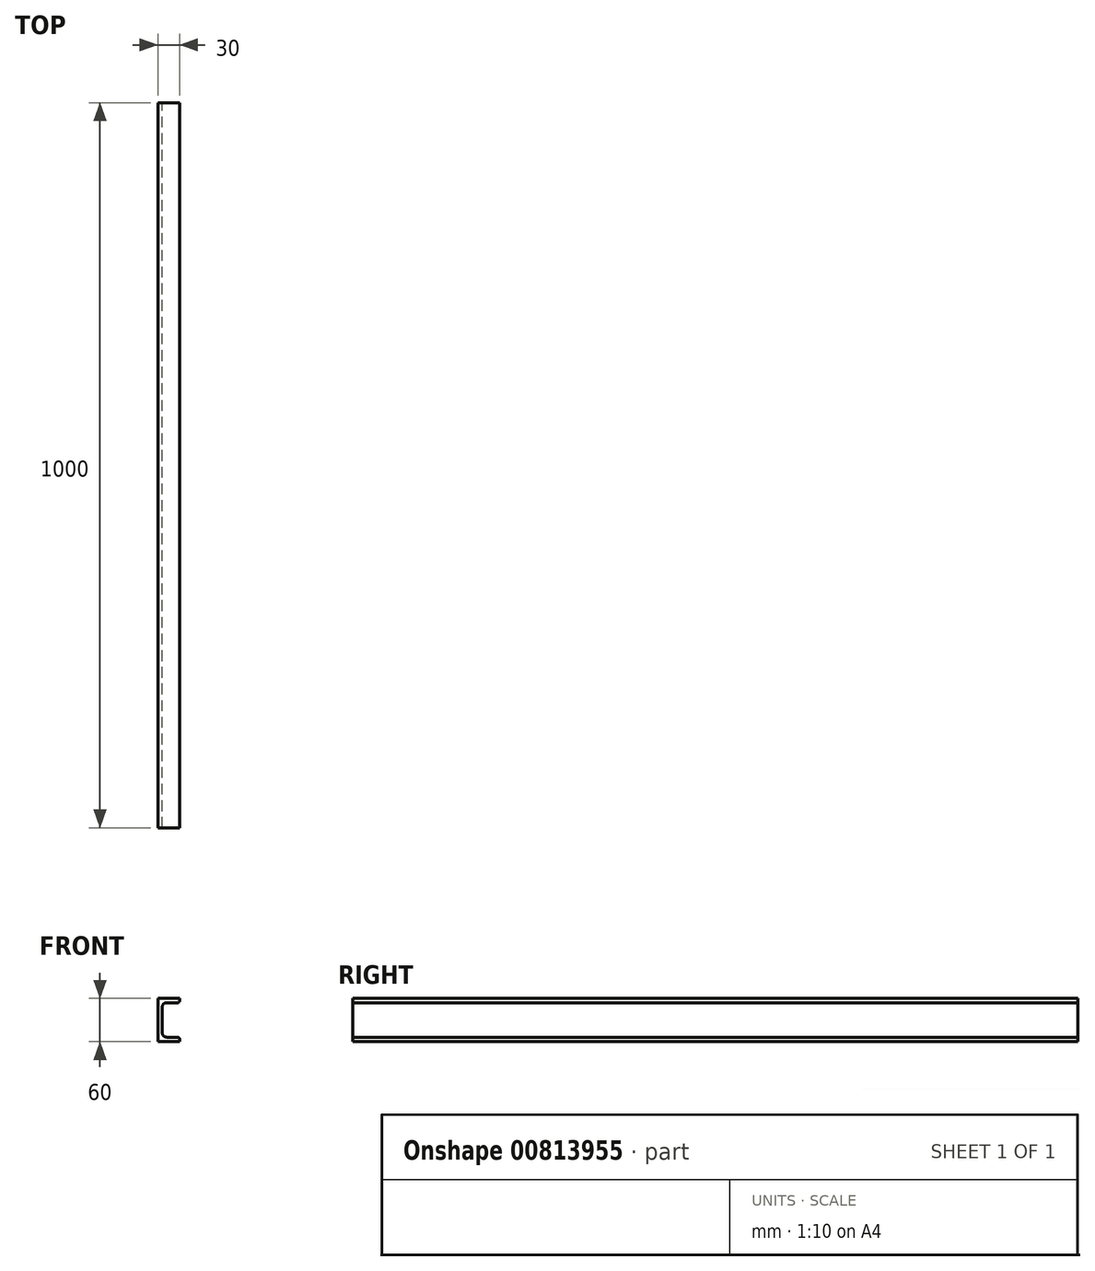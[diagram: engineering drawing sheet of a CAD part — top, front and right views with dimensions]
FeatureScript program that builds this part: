
annotation { "Feature Type Name" : "Feature", "Feature Type Description" : "" }
export const myFeature = defineFeature(function(context is Context, id is Id, definition is map)
    precondition{}
    {
        {
            var Q0;
            Q0=qCreatedBy(makeId("Front.planeOp"),FACE);
            var sketch = newSketch(context, id + "F0", { "sketchPlane" : qUnion([Q0])});
            skLineSegment(sketch, "E0", {"start": v(0, 0) * mm, "end": v(0, 60) * mm});
            skLineSegment(sketch, "E1", {"start": v(0, 60) * mm, "end": v(30, 60) * mm});
            skLineSegment(sketch, "E2", {"start": v(30, 60) * mm, "end": v(30, 56.75) * mm});
            skLineSegment(sketch, "E3", {"start": v(27, 53.75) * mm, "end": v(12, 53.75) * mm});
            skLineSegment(sketch, "E4", {"start": v(6, 47.75) * mm, "end": v(6, 12.25) * mm});
            skLineSegment(sketch, "E5", {"start": v(12, 6.25) * mm, "end": v(27, 6.25) * mm});
            skLineSegment(sketch, "E6", {"start": v(30, 3.25) * mm, "end": v(30, 0) * mm});
            skLineSegment(sketch, "E7", {"start": v(30, 0) * mm, "end": v(0, 0) * mm});
            skPoint(sketch, "E8.visualSharp", {"position": v(30, 53.75) * mm});
            skArc(sketch, "E8.filletArc", {"start": v(27, 53.75) * mm, "mid": v(29.12, 54.63) * mm, "end": v(30, 56.75) * mm});
            skPoint(sketch, "E9.visualSharp", {"position": v(6, 53.75) * mm});
            skArc(sketch, "E9.filletArc", {"start": v(12, 53.75) * mm, "mid": v(7.76, 52) * mm, "end": v(6, 47.75) * mm});
            skPoint(sketch, "E10.visualSharp", {"position": v(6, 6.25) * mm});
            skArc(sketch, "E10.filletArc", {"start": v(6, 12.25) * mm, "mid": v(7.76, 8) * mm, "end": v(12, 6.25) * mm});
            skPoint(sketch, "E11.visualSharp", {"position": v(30, 6.25) * mm});
            skArc(sketch, "E11.filletArc", {"start": v(30, 3.25) * mm, "mid": v(29.12, 5.37) * mm, "end": v(27, 6.25) * mm});
            skSolve(sketch);
        }
        {
            var Q0;
            Q0=makeQuery(id+"F0.imprint","IMPRINT",FACE,{"disambiguationData":[TD([[makeQuery(id+"F0.imprint","IMPRINT",EDGE,{"derivedFrom":sQuery(id+"F0.wireOp",EDGE,"E0")}),-1.0]])]});
            extrude(context, id + "F1", {"entities" : qUnion([Q0]), "endBound" : BoundingType.SYMMETRIC, "depth" : 1000 * mm, "offsetDistance" : 25 * mm});
        }
    });
